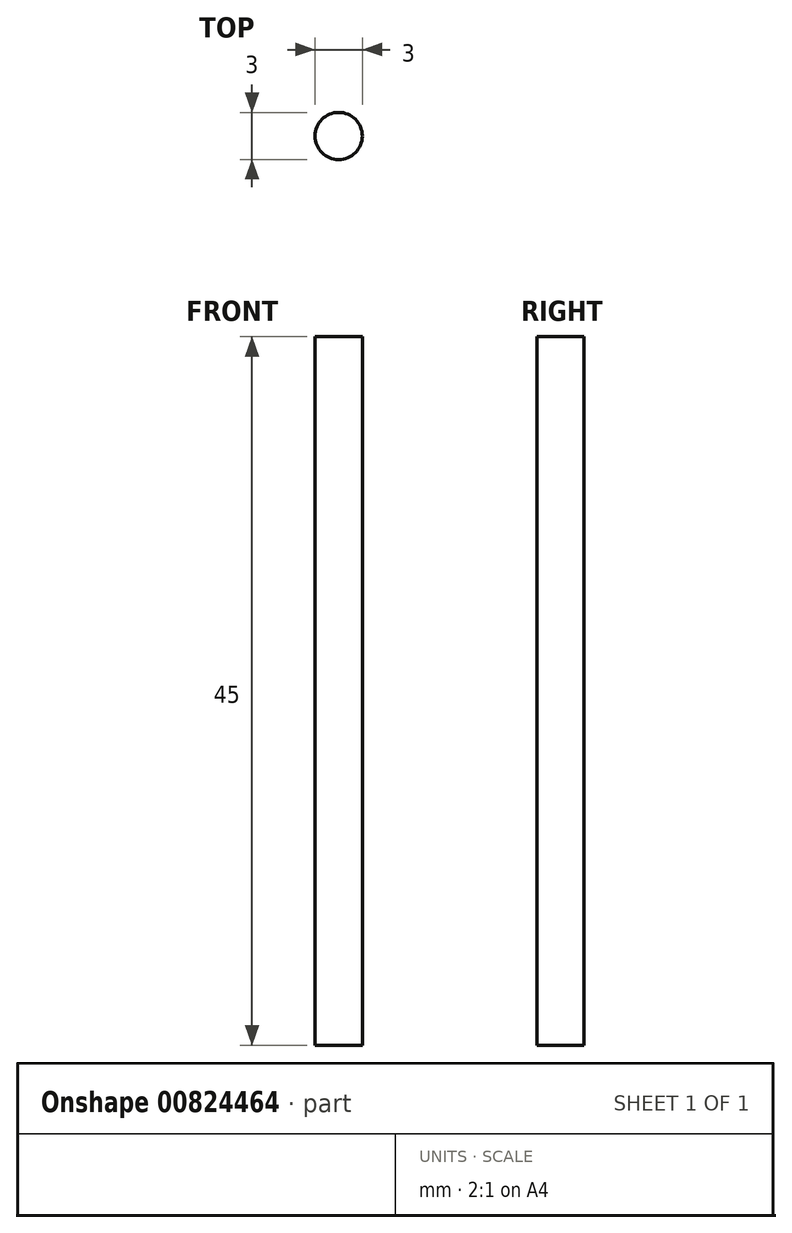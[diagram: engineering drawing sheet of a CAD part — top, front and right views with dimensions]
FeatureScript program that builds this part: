
annotation { "Feature Type Name" : "Feature", "Feature Type Description" : "" }
export const myFeature = defineFeature(function(context is Context, id is Id, definition is map)
    precondition{}
    {
        {
            var Q0;
            Q0=qCreatedBy(makeId("Top.planeOp"),FACE);
            var sketch = newSketch(context, id + "F0", { "sketchPlane" : qUnion([Q0])});
            skCircle(sketch, "E0", {"center": v(0, 0) * mm, "radius": 1.5 * mm});
            skSolve(sketch);
        }
        {
            var Q0;
            Q0 = qSketchRegion(id + "F0", true);
            extrude(context, id + "F1", {"entities" : qUnion([Q0]), "depth" : 45 * mm, "offsetDistance" : 25 * mm});
        }
    });
